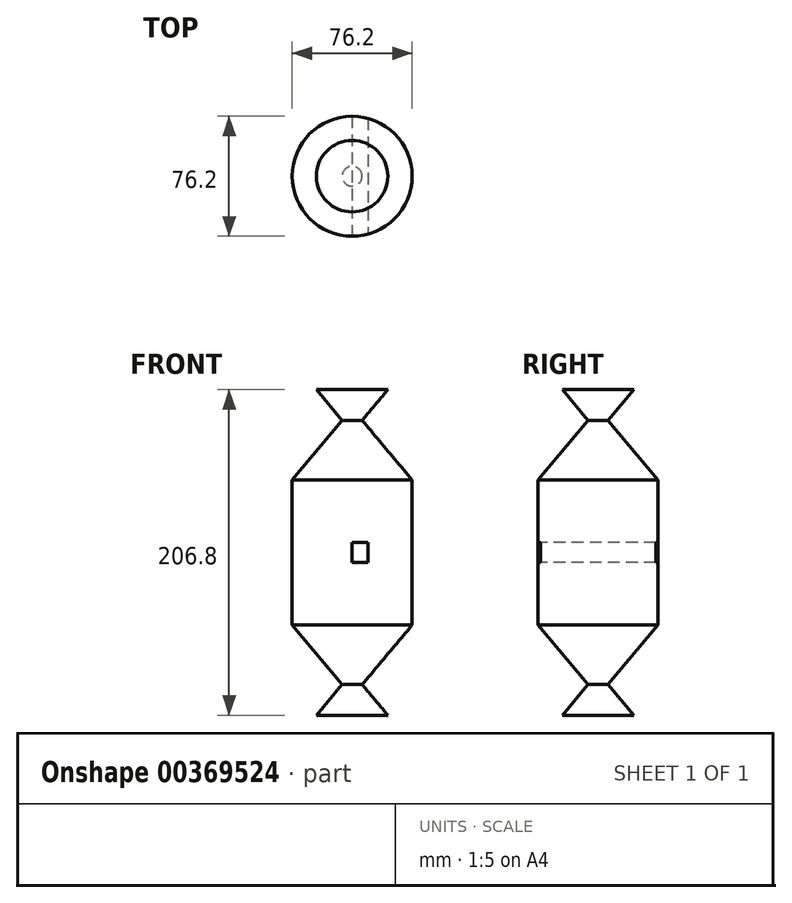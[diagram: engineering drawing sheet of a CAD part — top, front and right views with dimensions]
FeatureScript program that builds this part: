
annotation { "Feature Type Name" : "Feature", "Feature Type Description" : "" }
export const myFeature = defineFeature(function(context is Context, id is Id, definition is map)
    precondition{}
    {
        {
            var Q0;
            Q0=qCreatedBy(makeId("Front.planeOp"),FACE);
            var sketch = newSketch(context, id + "F0", { "sketchPlane" : qUnion([Q0])});
            skLineSegment(sketch, "E0", {"start": v(-38.1, 0) * mm, "end": v(-38.1, 46.1) * mm});
            skLineSegment(sketch, "E1", {"start": v(-38.1, 46.1) * mm, "end": v(-38.1, 46.1) * mm});
            skLineSegment(sketch, "E2", {"start": v(-38.1, 46.1) * mm, "end": v(0, 91.5) * mm});
            skLineSegment(sketch, "E3", {"start": v(0, 91.5) * mm, "end": v(0, 0) * mm, "construction": true});
            skLineSegment(sketch, "E4.MirrorCS", {"start": v(38.1, 46.1) * mm, "end": v(0, 91.5) * mm});
            skLineSegment(sketch, "E5.MirrorCS", {"start": v(38.1, 0) * mm, "end": v(38.1, 46.1) * mm});
            skLineSegment(sketch, "E6", {"start": v(-38.1, 0) * mm, "end": v(38.1, 0) * mm, "construction": true});
            skLineSegment(sketch, "E7.MirrorCS", {"start": v(-38.1, 0) * mm, "end": v(-38.1, -46.1) * mm});
            skLineSegment(sketch, "E8.MirrorCS", {"start": v(-38.1, -46.1) * mm, "end": v(0, -91.5) * mm});
            skLineSegment(sketch, "E9.MirrorCS", {"start": v(38.1, -46.1) * mm, "end": v(0, -91.5) * mm});
            skLineSegment(sketch, "E10.MirrorCS", {"start": v(38.1, 0) * mm, "end": v(38.1, -46.1) * mm});
            skLineSegment(sketch, "E11", {"start": v(-6.35, 83.94) * mm, "end": v(6.35, 83.94) * mm});
            skLineSegment(sketch, "E12", {"start": v(-6.35, 83.94) * mm, "end": v(-22.68, 103.4) * mm});
            skLineSegment(sketch, "E13.MirrorCS", {"start": v(6.35, 83.94) * mm, "end": v(22.68, 103.4) * mm});
            skLineSegment(sketch, "E14", {"start": v(-22.68, 103.4) * mm, "end": v(22.68, 103.4) * mm});
            skLineSegment(sketch, "E15.MirrorCS", {"start": v(6.35, -83.94) * mm, "end": v(22.68, -103.4) * mm});
            skLineSegment(sketch, "E16.MirrorCS", {"start": v(-6.35, -83.94) * mm, "end": v(-22.68, -103.4) * mm});
            skLineSegment(sketch, "E17.MirrorCS", {"start": v(-22.68, -103.4) * mm, "end": v(22.68, -103.4) * mm});
            skLineSegment(sketch, "E18", {"start": v(0, 103.4) * mm, "end": v(0, -103.4) * mm});
            skSolve(sketch);
        }
        {
            var Q0;
            {var subQ4=sQuery(id+"F0.wireOp",EDGE,"E0");Q0=makeQuery(id+"F0.imprint","IMPRINT",FACE,{"disambiguationData":[TD([[makeQuery(id+"F0.imprint","IMPRINT",EDGE,{"derivedFrom":subQ4}),-1.0]])]});}
            var Q1;
            {var subQ3=sQuery(id+"F0.wireOp",EDGE,"E12");Q1=makeQuery(id+"F0.imprint","IMPRINT",FACE,{"disambiguationData":[TD([[makeQuery(id+"F0.imprint","IMPRINT",EDGE,{"derivedFrom":subQ3}),-1.0]])]});}
            var Q2;
            {var subQ0=sQuery(id+"F0.wireOp",EDGE,"E18");var subQ3=sQuery(id+"F0.wireOp",EDGE,"E11");var subQ5=makeQuery(id+"F0.imprint","INTERSECT",VERTEX,{"derivedFrom":[subQ3,subQ0]});Q2=makeQuery(id+"F0.imprint","IMPRINT",FACE,{"disambiguationData":[TD([[makeQuery(id+"F0.imprint","IMPRINT",EDGE,{"disambiguationData":[TD([[subQ5,1.0]])],"derivedFrom":subQ3}),1.0]])]});}
            var Q3;
            {var subQ3=sQuery(id+"F0.wireOp",EDGE,"E16.MirrorCS");Q3=makeQuery(id+"F0.imprint","IMPRINT",FACE,{"disambiguationData":[TD([[makeQuery(id+"F0.imprint","IMPRINT",EDGE,{"derivedFrom":subQ3}),1.0]])]});}
            var Q4;
            Q4=sQuery(id+"F0.wireOp",EDGE,"E18");
            revolve(context, id + "F1", {"entities" : qUnion([Q0, Q1, Q2, Q3]), "axis" : qUnion([Q4]), "revolveType" : RevolveType.FULL});
        }
        {
            var Q0;
            Q0=qCreatedBy(makeId("Front.planeOp"),FACE);
            var sketch = newSketch(context, id + "F2", { "sketchPlane" : qUnion([Q0])});
            skLineSegment(sketch, "E19.bottom", {"start": v(-38.1, 6.35) * mm, "end": v(38.1, 6.35) * mm});
            skLineSegment(sketch, "E19.top", {"start": v(-38.1, -6.35) * mm, "end": v(38.1, -6.35) * mm});
            skLineSegment(sketch, "E19.left", {"start": v(-38.1, 6.35) * mm, "end": v(-38.1, -6.35) * mm});
            skLineSegment(sketch, "E19.right", {"start": v(38.1, 6.35) * mm, "end": v(38.1, -6.35) * mm});
            skLineSegment(sketch, "E20", {"start": v(0, 6.35) * mm, "end": v(0, -6.35) * mm});
            skLineSegment(sketch, "E21", {"start": v(10.16, 6.35) * mm, "end": v(10.16, -6.35) * mm});
            skPoint(sketch, "E22", {"position": v(0, 0) * mm});
            skSolve(sketch);
        }
        {
            var Q0;
            {var subQ0=sQuery(id+"F2.wireOp",EDGE,"E20");Q0=makeQuery(id+"F2.imprint","IMPRINT",FACE,{"disambiguationData":[TD([[makeQuery(id+"F2.imprint","IMPRINT",EDGE,{"derivedFrom":subQ0}),1.0]])]});}
            extrude(context, id + "F3", {"entities" : qUnion([Q0]), "operationType" : NewBodyOperationType.REMOVE, "endBound" : BoundingType.SYMMETRIC, "oppositeDirection" : true, "depth" : 76.2 * mm});
        }
    });
